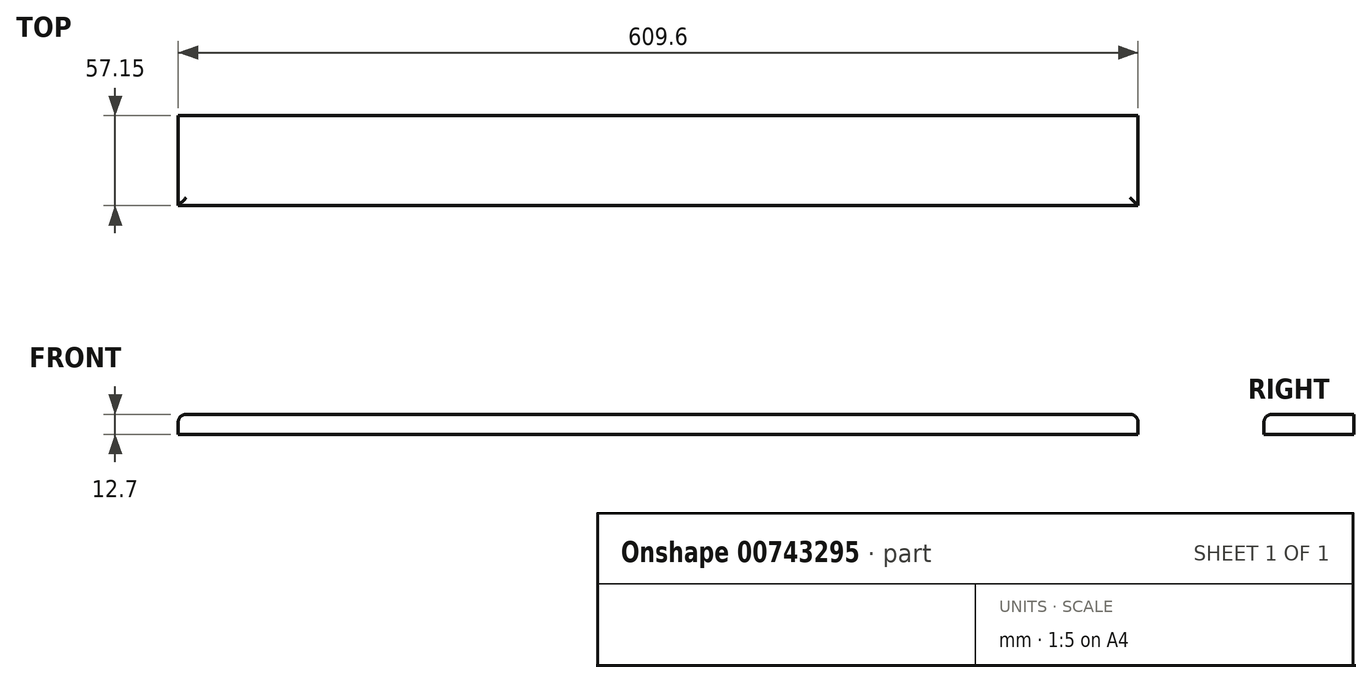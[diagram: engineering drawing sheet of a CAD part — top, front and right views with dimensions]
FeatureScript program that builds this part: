
annotation { "Feature Type Name" : "Feature", "Feature Type Description" : "" }
export const myFeature = defineFeature(function(context is Context, id is Id, definition is map)
    precondition{}
    {
        {
            var Q0;
            Q0=qCreatedBy(makeId("Top.planeOp"),FACE);
            var sketch = newSketch(context, id + "F0", { "sketchPlane" : qUnion([Q0])});
            skLineSegment(sketch, "E0.bottom", {"start": v(-609.6, 57.15) * mm, "end": v(0, 57.15) * mm});
            skLineSegment(sketch, "E0.top", {"start": v(-609.6, 0) * mm, "end": v(0, 0) * mm});
            skLineSegment(sketch, "E0.left", {"start": v(-609.6, 57.15) * mm, "end": v(-609.6, 0) * mm});
            skLineSegment(sketch, "E0.right", {"start": v(0, 57.15) * mm, "end": v(0, 0) * mm});
            skSolve(sketch);
        }
        {
            var Q0;
            Q0=makeQuery(id+"F0.imprint","IMPRINT",FACE,{"disambiguationData":[TD([[makeQuery(id+"F0.imprint","IMPRINT",EDGE,{"derivedFrom":sQuery(id+"F0.wireOp",EDGE,"E0.bottom")}),-1.0]])]});
            extrude(context, id + "F1", {"entities" : qUnion([Q0]), "depth" : 12.7 * mm});
        }
        {
            var Q0;
            Q0=makeQuery(id+"F1.opExtrude","CAP_EDGE",EDGE,{"disambiguationData":[OSD([sQuery(id+"F0.wireOp",EDGE,"E0.top")])],"isStart":false});
            var Q1;
            Q1=makeQuery(id+"F1.opExtrude","CAP_EDGE",EDGE,{"disambiguationData":[OSD([sQuery(id+"F0.wireOp",EDGE,"E0.left")])],"isStart":false});
            var Q2;
            Q2=makeQuery(id+"F1.opExtrude","CAP_EDGE",EDGE,{"disambiguationData":[OSD([sQuery(id+"F0.wireOp",EDGE,"E0.right")])],"isStart":false});
            fillet(context, id + "F2", {"entities" : qUnion([Q0, Q1, Q2]), "radius" : 5.08 * mm, "tangentPropagation" : true, "allowEdgeOverflow" : false});
        }
    });
